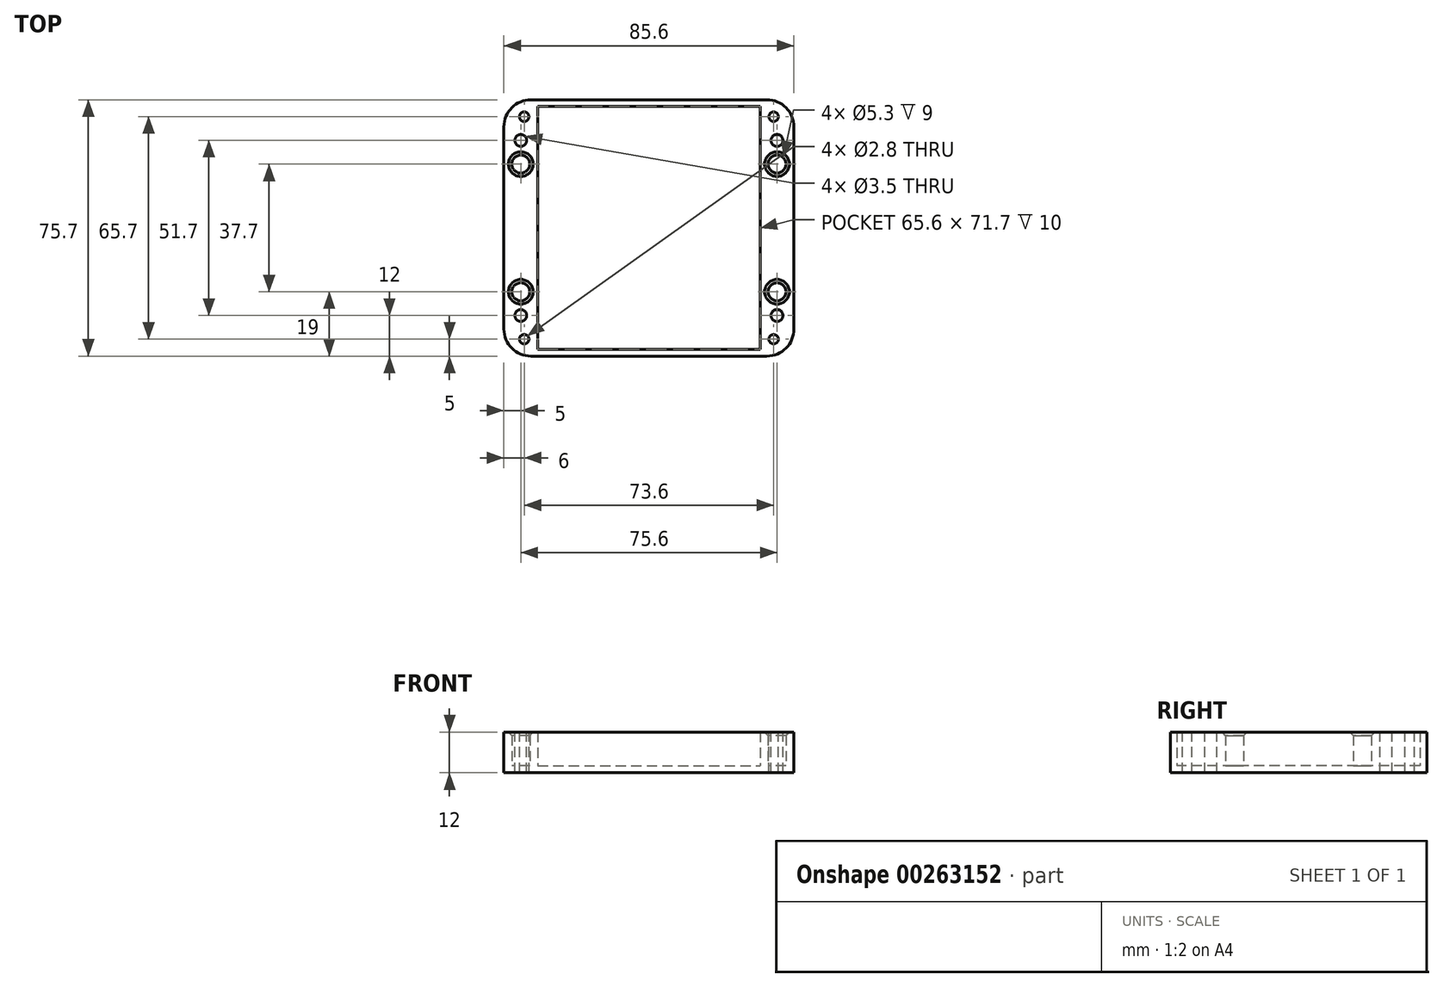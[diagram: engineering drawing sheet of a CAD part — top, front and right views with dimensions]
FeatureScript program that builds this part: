
annotation { "Feature Type Name" : "Feature", "Feature Type Description" : "" }
export const myFeature = defineFeature(function(context is Context, id is Id, definition is map)
    precondition{}
    {
        {
            var Q0;
            Q0=qCreatedBy(makeId("Top.planeOp"),FACE);
            var sketch = newSketch(context, id + "F0", { "sketchPlane" : qUnion([Q0])});
            skLineSegment(sketch, "E0.bottom", {"start": v(-34.8, 37.85) * mm, "end": v(34.8, 37.85) * mm});
            skLineSegment(sketch, "E0.top", {"start": v(-34.8, -37.85) * mm, "end": v(34.8, -37.85) * mm});
            skLineSegment(sketch, "E1.bottom", {"start": v(-32.3, 35.35) * mm, "end": v(32.3, 35.35) * mm, "construction": true});
            skLineSegment(sketch, "E1.top", {"start": v(-32.3, -35.35) * mm, "end": v(32.3, -35.35) * mm, "construction": true});
            skLineSegment(sketch, "E1.left", {"start": v(-32.3, 35.35) * mm, "end": v(-32.3, -35.35) * mm, "construction": true});
            skLineSegment(sketch, "E1.right", {"start": v(32.3, 35.35) * mm, "end": v(32.3, -35.35) * mm, "construction": true});
            skLineSegment(sketch, "E2", {"start": v(-42.8, 29.85) * mm, "end": v(-42.8, -29.85) * mm});
            skLineSegment(sketch, "E3", {"start": v(42.8, 29.85) * mm, "end": v(42.8, -29.85) * mm});
            skArc(sketch, "E4", {"start": v(-34.8, 37.85) * mm, "mid": v(-40.46, 35.5) * mm, "end": v(-42.8, 29.85) * mm});
            skArc(sketch, "E5", {"start": v(42.8, 29.85) * mm, "mid": v(40.46, 35.5) * mm, "end": v(34.8, 37.85) * mm});
            skArc(sketch, "E6", {"start": v(34.8, -37.85) * mm, "mid": v(40.46, -35.5) * mm, "end": v(42.8, -29.85) * mm});
            skArc(sketch, "E7", {"start": v(-42.8, -29.85) * mm, "mid": v(-40.46, -35.5) * mm, "end": v(-34.8, -37.85) * mm});
            skSolve(sketch);
        }
        {
            var Q0;
            Q0 = qSketchRegion(id + "F0", true);
            extrude(context, id + "F1", {"entities" : qUnion([Q0]), "depth" : 2 * mm});
        }
        {
            var Q0;
            Q0=makeQuery(id+"F1.opExtrude","CAP_FACE",FACE,{"disambiguationData":[OSD([sQuery(id+"F0.wireOp",EDGE,"E0.bottom"),sQuery(id+"F0.wireOp",EDGE,"E0.top"),sQuery(id+"F0.wireOp",EDGE,"E2"),sQuery(id+"F0.wireOp",EDGE,"E3"),sQuery(id+"F0.wireOp",EDGE,"E4"),sQuery(id+"F0.wireOp",EDGE,"E5"),sQuery(id+"F0.wireOp",EDGE,"E6"),sQuery(id+"F0.wireOp",EDGE,"E7")])],"isStart":false});
            var sketch = newSketch(context, id + "F2", { "sketchPlane" : qUnion([Q0])});
            skLineSegment(sketch, "E8", {"start": v(-42.8, 29.85) * mm, "end": v(-42.8, -29.85) * mm});
            skLineSegment(sketch, "E9", {"start": v(-34.8, 37.85) * mm, "end": v(34.8, 37.85) * mm});
            skLineSegment(sketch, "E10", {"start": v(42.8, 29.85) * mm, "end": v(42.8, -29.85) * mm});
            skLineSegment(sketch, "E11", {"start": v(-34.8, -37.85) * mm, "end": v(34.8, -37.85) * mm});
            skArc(sketch, "E12", {"start": v(-42.8, -29.85) * mm, "mid": v(-40.46, -35.5) * mm, "end": v(-34.8, -37.85) * mm});
            skArc(sketch, "E13", {"start": v(-34.8, 37.85) * mm, "mid": v(-40.46, 35.5) * mm, "end": v(-42.8, 29.85) * mm});
            skArc(sketch, "E14", {"start": v(42.8, 29.85) * mm, "mid": v(40.46, 35.5) * mm, "end": v(34.8, 37.85) * mm});
            skArc(sketch, "E15", {"start": v(34.8, -37.85) * mm, "mid": v(40.46, -35.5) * mm, "end": v(42.8, -29.85) * mm});
            skLineSegment(sketch, "E16.bottom", {"start": v(-32.8, 35.85) * mm, "end": v(32.8, 35.85) * mm});
            skLineSegment(sketch, "E16.top", {"start": v(-32.8, -35.85) * mm, "end": v(32.8, -35.85) * mm});
            skLineSegment(sketch, "E16.left", {"start": v(-32.8, 35.85) * mm, "end": v(-32.8, -35.85) * mm});
            skLineSegment(sketch, "E16.right", {"start": v(32.8, 35.85) * mm, "end": v(32.8, -35.85) * mm});
            skLineSegment(sketch, "E17", {"start": v(-42.8, -29.85) * mm, "end": v(-34.8, -29.85) * mm, "construction": true});
            skCircle(sketch, "E18", {"center": v(-37.8, -18.85) * mm, "radius": 2.65 * mm});
            skCircle(sketch, "E19.MirrorC", {"center": v(37.8, -18.85) * mm, "radius": 2.65 * mm});
            skCircle(sketch, "E20.MirrorC", {"center": v(-37.8, 18.85) * mm, "radius": 2.65 * mm});
            skCircle(sketch, "E21.MirrorC", {"center": v(37.8, 18.85) * mm, "radius": 2.65 * mm});
            skSolve(sketch);
        }
        {
            var Q0;
            Q0 = qSketchRegion(id + "F2", true);
            extrude(context, id + "F3", {"entities" : qUnion([Q0]), "operationType" : NewBodyOperationType.ADD, "depth" : 10 * mm});
        }
        {
            var Q0;
            Q0=makeQuery(id+"F3.opExtrude","CAP_FACE",FACE,{"disambiguationData":[OSD([sQuery(id+"F2.wireOp",EDGE,"E8"),sQuery(id+"F2.wireOp",EDGE,"E9"),sQuery(id+"F2.wireOp",EDGE,"E10"),sQuery(id+"F2.wireOp",EDGE,"E11"),sQuery(id+"F2.wireOp",EDGE,"E12"),sQuery(id+"F2.wireOp",EDGE,"E13"),sQuery(id+"F2.wireOp",EDGE,"E14"),sQuery(id+"F2.wireOp",EDGE,"E15"),sQuery(id+"F2.wireOp",EDGE,"E16.bottom"),sQuery(id+"F2.wireOp",EDGE,"E16.top"),sQuery(id+"F2.wireOp",EDGE,"E16.left"),sQuery(id+"F2.wireOp",EDGE,"E16.right")])],"isStart":false});
            var sketch = newSketch(context, id + "F4", { "sketchPlane" : qUnion([Q0])});
            skCircle(sketch, "E22", {"center": v(-36.8, -32.85) * mm, "radius": 1.4 * mm});
            skCircle(sketch, "E23.MirrorC", {"center": v(36.8, -32.85) * mm, "radius": 1.4 * mm});
            skCircle(sketch, "E24.MirrorC", {"center": v(-36.8, 32.85) * mm, "radius": 1.4 * mm});
            skCircle(sketch, "E25.MirrorC", {"center": v(36.8, 32.85) * mm, "radius": 1.4 * mm});
            skCircle(sketch, "E26", {"center": v(-37.8, -25.85) * mm, "radius": 1.75 * mm});
            skCircle(sketch, "E27.MirrorC", {"center": v(37.8, -25.85) * mm, "radius": 1.75 * mm});
            skCircle(sketch, "E28.MirrorC", {"center": v(-37.8, 25.85) * mm, "radius": 1.75 * mm});
            skCircle(sketch, "E29.MirrorC", {"center": v(37.8, 25.85) * mm, "radius": 1.75 * mm});
            skSolve(sketch);
        }
        {
            var Q0;
            Q0 = qSketchRegion(id + "F4", true);
            var Q1;
            Q1=makeQuery(id+"F1.opExtrude","CAP_FACE",FACE,{"disambiguationData":[OSD([sQuery(id+"F0.wireOp",EDGE,"E0.bottom"),sQuery(id+"F0.wireOp",EDGE,"E0.top"),sQuery(id+"F0.wireOp",EDGE,"E2"),sQuery(id+"F0.wireOp",EDGE,"E3"),sQuery(id+"F0.wireOp",EDGE,"E4"),sQuery(id+"F0.wireOp",EDGE,"E5"),sQuery(id+"F0.wireOp",EDGE,"E6"),sQuery(id+"F0.wireOp",EDGE,"E7")])],"isStart":true});
            extrude(context, id + "F5", {"entities" : qUnion([Q0]), "operationType" : NewBodyOperationType.REMOVE, "endBound" : BoundingType.UP_TO_SURFACE, "oppositeDirection" : true, "endBoundEntityFace" : qUnion([Q1]), "depth" : 25 * mm});
        }
        {
            var Q0;
            Q0=makeQuery(id+"F3.opExtrude","CAP_EDGE",EDGE,{"disambiguationData":[OSD([sQuery(id+"F2.wireOp",EDGE,"E20.MirrorC")])],"isStart":false});
            var Q1;
            Q1=makeQuery(id+"F3.opExtrude","CAP_EDGE",EDGE,{"disambiguationData":[OSD([sQuery(id+"F2.wireOp",EDGE,"E21.MirrorC")])],"isStart":false});
            var Q2;
            Q2=makeQuery(id+"F3.opExtrude","CAP_EDGE",EDGE,{"disambiguationData":[OSD([sQuery(id+"F2.wireOp",EDGE,"E19.MirrorC")])],"isStart":false});
            var Q3;
            Q3=makeQuery(id+"F3.opExtrude","CAP_EDGE",EDGE,{"disambiguationData":[OSD([sQuery(id+"F2.wireOp",EDGE,"E18")])],"isStart":false});
            chamfer(context, id + "F6", {"entities" : qUnion([Q0, Q1, Q2, Q3]), "width" : 1 * mm, "tangentPropagation" : true});
        }
    });
